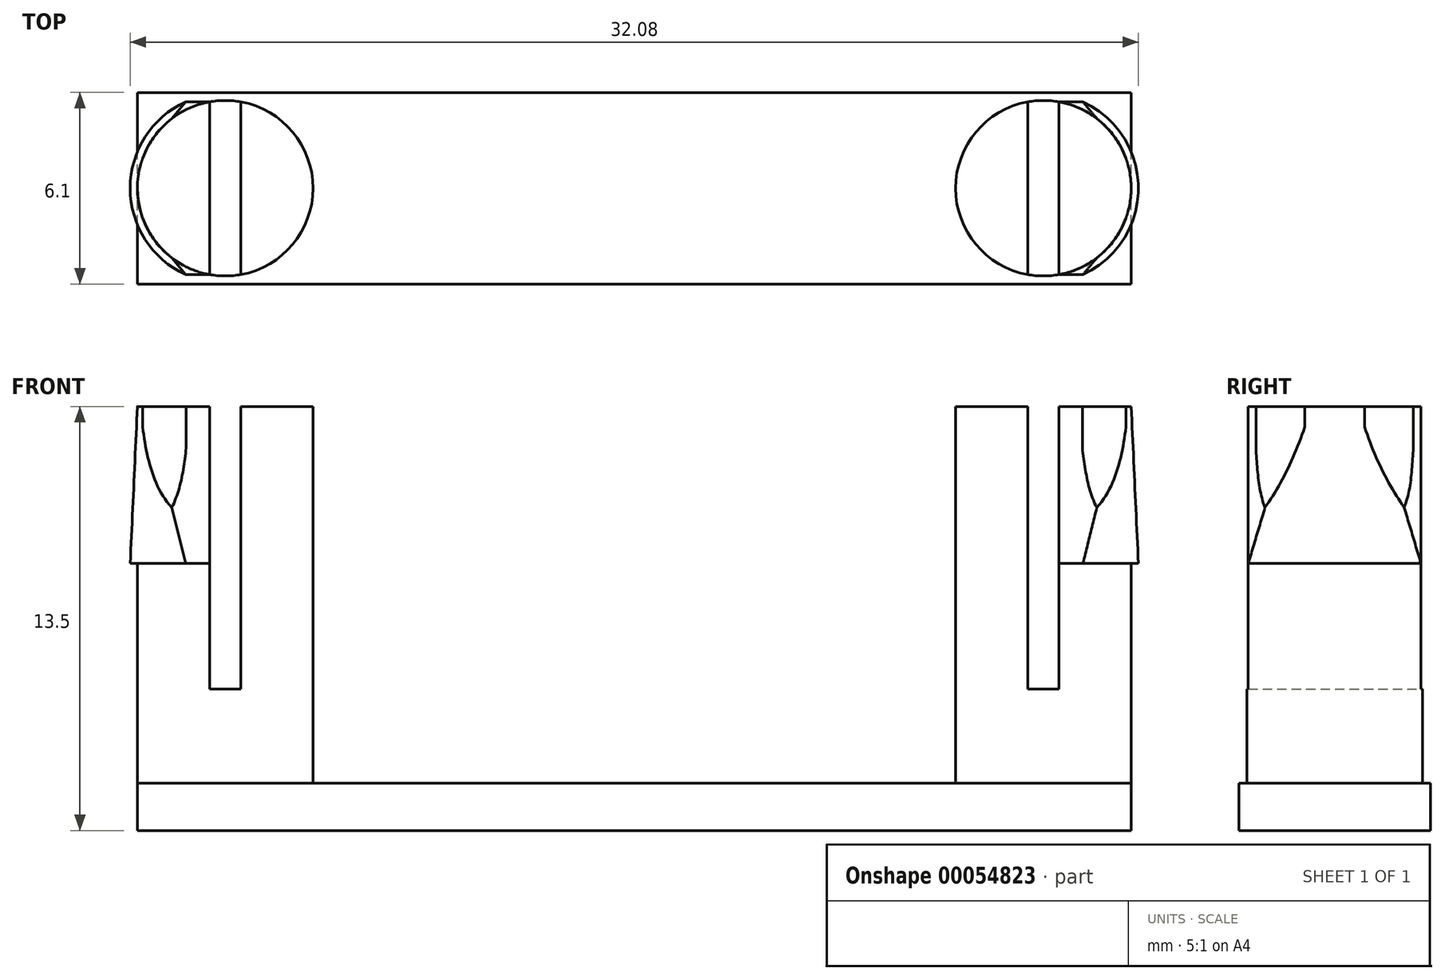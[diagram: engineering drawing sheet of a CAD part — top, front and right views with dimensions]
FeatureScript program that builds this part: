
annotation { "Feature Type Name" : "Feature", "Feature Type Description" : "" }
export const myFeature = defineFeature(function(context is Context, id is Id, definition is map)
    precondition{}
    {
        {
            var Q0;
            Q0=qCreatedBy(makeId("Top.planeOp"),FACE);
            var sketch = newSketch(context, id + "F0", { "sketchPlane" : qUnion([Q0])});
            skLineSegment(sketch, "E0.bottom", {"start": v(0, 0) * mm, "end": v(31.62, 0) * mm});
            skLineSegment(sketch, "E0.top", {"start": v(0, 6.1) * mm, "end": v(31.62, 6.1) * mm});
            skLineSegment(sketch, "E0.left", {"start": v(0, 0) * mm, "end": v(0, 6.1) * mm});
            skLineSegment(sketch, "E0.right", {"start": v(31.62, 0) * mm, "end": v(31.62, 6.1) * mm});
            skSolve(sketch);
        }
        {
            var Q0;
            Q0 = qSketchRegion(id + "F0", true);
            extrude(context, id + "F1", {"entities" : qUnion([Q0]), "depth" : 1.5 * mm});
        }
        {
            var Q0;
            Q0=makeQuery(id+"F1.opExtrude","CAP_FACE",FACE,{"disambiguationData":[OSD([sQuery(id+"F0.wireOp",EDGE,"E0.bottom"),sQuery(id+"F0.wireOp",EDGE,"E0.top"),sQuery(id+"F0.wireOp",EDGE,"E0.left"),sQuery(id+"F0.wireOp",EDGE,"E0.right")])],"isStart":false});
            var sketch = newSketch(context, id + "F2", { "sketchPlane" : qUnion([Q0])});
            skLineSegment(sketch, "E1", {"start": v(2.8, 3.05) * mm, "end": v(0, 3.05) * mm, "construction": true});
            skPoint(sketch, "E2.orphan", {"position": v(31.62, 6.1) * mm});
            skPoint(sketch, "E3.orphan", {"position": v(31.62, 0) * mm});
            skPoint(sketch, "E4.orphan", {"position": v(0, 0) * mm});
            skPoint(sketch, "E5.orphan", {"position": v(0, 6.1) * mm});
            skCircle(sketch, "E6", {"center": v(2.8, 3.05) * mm, "radius": 2.8 * mm});
            skSolve(sketch);
        }
        {
            var Q0;
            Q0 = qSketchRegion(id + "F2", true);
            extrude(context, id + "F3", {"entities" : qUnion([Q0]), "operationType" : NewBodyOperationType.ADD, "depth" : 12 * mm});
        }
        {
            var Q0;
            Q0=makeQuery(id+"F3.opExtrude","CAP_FACE",FACE,{"disambiguationData":[OSD([sQuery(id+"F2.wireOp",EDGE,"E6")])],"isStart":false});
            var sketch = newSketch(context, id + "F4", { "sketchPlane" : qUnion([Q0])});
            skLineSegment(sketch, "E7.bottom", {"start": v(2.3, 0) * mm, "end": v(3.3, 0) * mm});
            skLineSegment(sketch, "E7.top", {"start": v(2.3, 6.1) * mm, "end": v(3.3, 6.1) * mm});
            skLineSegment(sketch, "E7.left", {"start": v(2.3, 0) * mm, "end": v(2.3, 6.1) * mm});
            skLineSegment(sketch, "E7.right", {"start": v(3.3, 0) * mm, "end": v(3.3, 6.1) * mm});
            skLineSegment(sketch, "E8", {"start": v(0, 3.02) * mm, "end": v(2.3, 3.02) * mm, "construction": true});
            skLineSegment(sketch, "E9", {"start": v(3.3, 3.02) * mm, "end": v(5.59, 3.02) * mm, "construction": true});
            skSolve(sketch);
        }
        {
            var Q0;
            Q0 = qSketchRegion(id + "F4", true);
            extrude(context, id + "F5", {"entities" : qUnion([Q0]), "operationType" : NewBodyOperationType.REMOVE, "oppositeDirection" : true, "depth" : 9 * mm});
        }
        {
            var Q0;
            {var subQ0=sQuery(id+"F0.wireOp",EDGE,"E0.right");var subQ1=sQuery(id+"F0.wireOp",EDGE,"E0.top");var subQ2=sQuery(id+"F0.wireOp",EDGE,"E0.bottom");Q0=makeQuery(id+"F3.boolean.opBoolean","SPLIT",FACE,{"disambiguationData":[TD([makeQuery(id+"F1.opExtrude","SWEPT_FACE",FACE,{"disambiguationData":[OSD([subQ2])]}),makeQuery(id+"F1.opExtrude","SWEPT_FACE",FACE,{"disambiguationData":[OSD([subQ1])]}),makeQuery(id+"F1.opExtrude","SWEPT_FACE",FACE,{"disambiguationData":[OSD([subQ0])]}),makeQuery(id+"F3.opExtrude","SWEPT_FACE",FACE,{"disambiguationData":[OSD([sQuery(id+"F2.wireOp",EDGE,"57f3152a-971c-4848-b1f8-9178880c2aee")])]}),makeQuery(id+"F3.opExtrude","SWEPT_FACE",FACE,{"disambiguationData":[OSD([sQuery(id+"F2.wireOp",EDGE,"2b9dea67-78c8-44f6-97de-ef6971056f3a.0")])]}),makeQuery(id+"F3.opExtrude","SWEPT_FACE",FACE,{"disambiguationData":[OSD([sQuery(id+"F2.wireOp",EDGE,"2b9dea67-78c8-44f6-97de-ef6971056f3a.1")])]})])],"derivedFrom":makeQuery(id+"F1.opExtrude","CAP_FACE",FACE,{"disambiguationData":[OSD([subQ2,subQ1,sQuery(id+"F0.wireOp",EDGE,"E0.left"),subQ0])],"isStart":false})});}
            cPlane(context, id + "F6", {"entities" : qUnion([Q0]), "cplaneType" : CPlaneType.OFFSET, "offset" : 7 * mm, "width" : 152.4 * mm, "height" : 152.4 * mm});
        }
        {
            var Q0;
            Q0=qCreatedBy(id+"F6.planeOp",FACE);
            var sketch = newSketch(context, id + "F7", { "sketchPlane" : qUnion([Q0])});
            skArc(sketch, "E10", {"start": v(1.53, 5.8) * mm, "mid": v(-0.23, 3.05) * mm, "end": v(1.53, 0.3) * mm});
            skLineSegment(sketch, "E11", {"start": v(2.3, 5.8) * mm, "end": v(1.53, 5.8) * mm});
            skArc(sketch, "E12.0", {"start": v(2.3, 5.8) * mm, "mid": v(0, 3.05) * mm, "end": v(2.3, 0.3) * mm});
            skLineSegment(sketch, "E13", {"start": v(1.53, 0.3) * mm, "end": v(2.3, 0.3) * mm});
            skSolve(sketch);
        }
        {
            var Q1;
            {var subQ0=sQuery(id+"F2.wireOp",EDGE,"E6");Q1=makeQuery(id+"F5.boolean.opBoolean","SPLIT",FACE,{"disambiguationData":[TD([makeQuery(id+"F5.opExtrude","SWEPT_FACE",FACE,{"disambiguationData":[OSD([sQuery(id+"F4.wireOp",EDGE,"E7.left")])]})])],"derivedFrom":makeQuery(id+"F3.opExtrude","CAP_FACE",FACE,{"disambiguationData":[OSD([subQ0])],"isStart":false})});}
            var Q2;
            Q2 = qSketchRegion(id + "F7", true);
            loft(context, id + "F8", {"operationType" : NewBodyOperationType.ADD, "sheetProfilesArray" : [{ "sheetProfileEntities" : qUnion([Q1]) }, { "sheetProfileEntities" : qUnion([Q2]) }]});
        }
        {
            var Q0;
            Q0=makeQuery(id+"F1.opExtrude","SWEPT_FACE",FACE,{"disambiguationData":[OSD([sQuery(id+"F0.wireOp",EDGE,"E0.left")])]});
            var Q1;
            Q1=makeQuery(id+"F1.opExtrude","SWEPT_FACE",FACE,{"disambiguationData":[OSD([sQuery(id+"F0.wireOp",EDGE,"E0.right")])]});
            cPlane(context, id + "F9", {"entities" : qUnion([Q0, Q1]), "cplaneType" : CPlaneType.MID_PLANE, "offset" : 152.4 * mm, "width" : 152.4 * mm, "height" : 152.4 * mm});
        }
        {
            var Q0;
            Q0=makeQuery(id+"F1.opExtrude","SWEPT_BODY",BODY,{"disambiguationData":[OSD([sQuery(id+"F0.wireOp",EDGE,"E0.bottom"),sQuery(id+"F0.wireOp",EDGE,"E0.top"),sQuery(id+"F0.wireOp",EDGE,"E0.left"),sQuery(id+"F0.wireOp",EDGE,"E0.right")])]});
            var Q1;
            Q1=qCreatedBy(id+"F9.planeOp",FACE);
            mirror(context, id + "F10", {"operationType" : NewBodyOperationType.ADD, "entities" : qUnion([Q0]), "mirrorPlane" : qUnion([Q1])});
        }
    });
